FCSTD DOCUMENT  (FreeCAD 0.16R6712 (Git))
Label: edc-mux-board-housing
License: All rights reserved
LicenseURL: http://en.wikipedia.org/wiki/All_rights_reserved
objects: Sketcher::SketchObject×1
note: 1 computed .brp shape members not serialized (recipe doc carries the construction recipe); baked Part::Feature solids carry a one-line shape summary decoded from their .brp

FEATURE [Sketcher::SketchObject] Sketch
  sketch-geometry (4):
    g0: LineSegment StartX=-47.0672 StartY=106.93 StartZ=0 EndX=43.2968 EndY=106.93 EndZ=0
    g1: LineSegment StartX=43.2968 StartY=106.93 StartZ=0 EndX=43.2968 EndY=-113.258 EndZ=0
    g2: LineSegment StartX=43.2968 StartY=-113.258 StartZ=0 EndX=-47.0672 EndY=-113.258 EndZ=0
    g3: LineSegment StartX=-47.0672 StartY=-113.258 StartZ=0 EndX=-47.0672 EndY=106.93 EndZ=0
  constraints (8):
    c: Coincident(g0,g1)
    c: Coincident(g1,g2)
    c: Coincident(g2,g3)
    c: Coincident(g3,g0)
    c: Horizontal(g0)
    c: Horizontal(g2)
    c: Vertical(g1)
    c: Vertical(g3)
